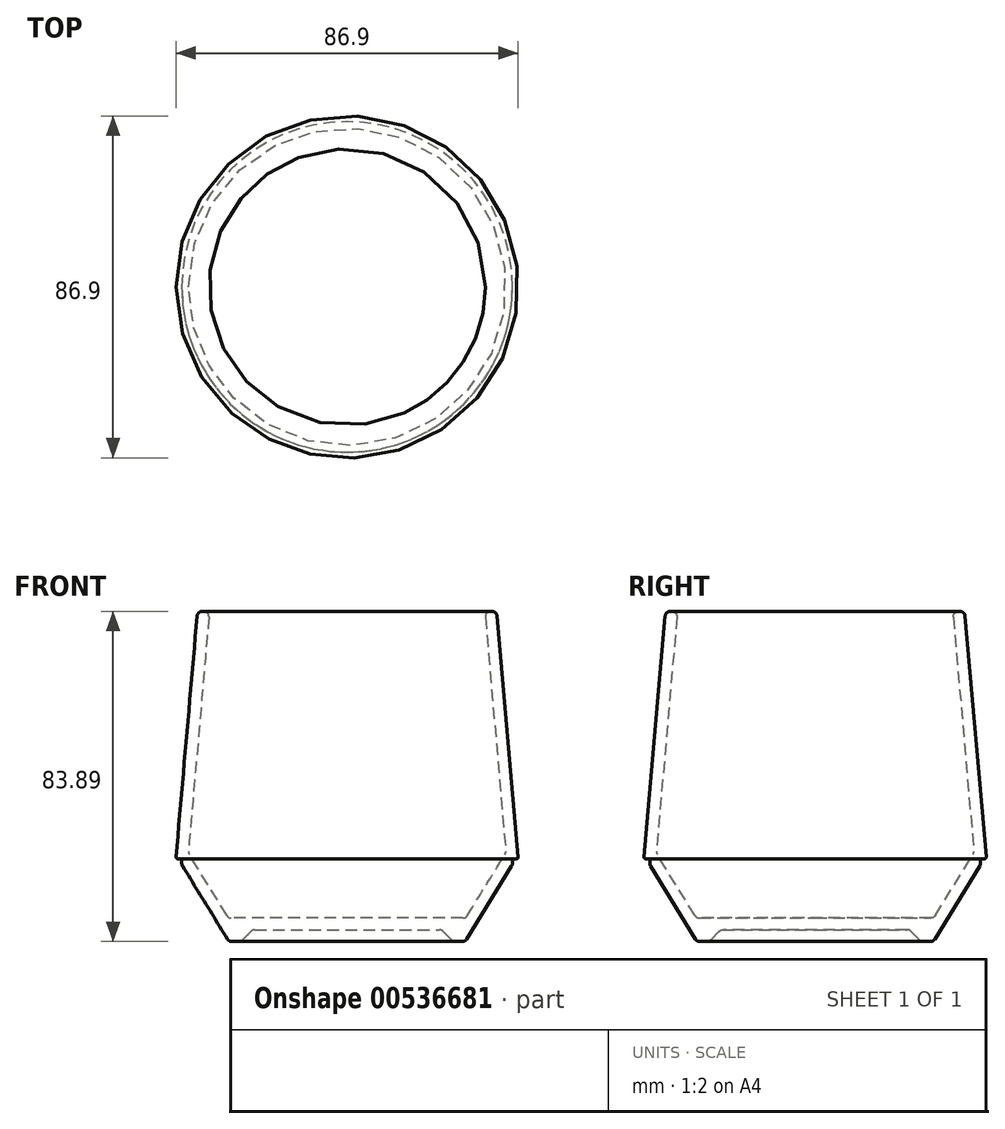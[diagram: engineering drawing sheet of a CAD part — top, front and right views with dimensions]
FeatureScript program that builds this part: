
annotation { "Feature Type Name" : "Feature", "Feature Type Description" : "" }
export const myFeature = defineFeature(function(context is Context, id is Id, definition is map)
    precondition{}
    {
        {
            var Q0;
            Q0=qCreatedBy(makeId("Front.planeOp"),FACE);
            var sketch = newSketch(context, id + "F0", { "sketchPlane" : qUnion([Q0])});
            skLineSegment(sketch, "E0", {"start": v(0, 3) * mm, "end": v(24, 3) * mm});
            skLineSegment(sketch, "E1", {"start": v(24, 3) * mm, "end": v(27, 0) * mm});
            skLineSegment(sketch, "E2", {"start": v(27, 0) * mm, "end": v(30, 0) * mm});
            skLineSegment(sketch, "E3", {"start": v(30, 0) * mm, "end": v(42, 19.5) * mm});
            skLineSegment(sketch, "E4", {"start": v(43.5, 21) * mm, "end": v(37.99, 84) * mm});
            skLineSegment(sketch, "E5", {"start": v(35, 83.74) * mm, "end": v(40.35, 22.55) * mm});
            skLineSegment(sketch, "E6", {"start": v(40.35, 22.55) * mm, "end": v(30.17, 6) * mm});
            skLineSegment(sketch, "E7", {"start": v(30.17, 6) * mm, "end": v(0, 6) * mm});
            skLineSegment(sketch, "E8", {"start": v(0, 6) * mm, "end": v(0, 3) * mm});
            skPoint(sketch, "E9.visualSharp", {"position": v(24, 3) * mm});
            skPoint(sketch, "E10.visualSharp", {"position": v(40.35, 22.55) * mm});
            skLineSegment(sketch, "E11", {"start": v(0, 0) * mm, "end": v(0, 84) * mm, "construction": true});
            skLineSegment(sketch, "E12", {"start": v(42, 19.5) * mm, "end": v(42, 21) * mm});
            skLineSegment(sketch, "E13", {"start": v(43.5, 0) * mm, "end": v(43.5, 84) * mm, "construction": true});
            skLineSegment(sketch, "E14", {"start": v(35, 83.74) * mm, "end": v(37.99, 84) * mm});
            skLineSegment(sketch, "E15", {"start": v(42, 21) * mm, "end": v(43.5, 21) * mm});
            skSolve(sketch);
        }
        {
            var Q0;
            Q0=qSketchRegion(id+"F0",true);
            var Q1;
            Q1=sQuery(id+"F0.wireOp",EDGE,"E11");
            revolve(context, id + "F1", {"entities" : qUnion([Q0]), "axis" : qUnion([Q1]), "revolveType" : RevolveType.FULL});
        }
        {
            var Q0;
            Q0=makeQuery(id+"F1.opRevolve","SWEPT_EDGE",EDGE,{"disambiguationData":[OSD([sQuery(id+"F0.wireOp",EDGE,"E5"),sQuery(id+"F0.wireOp",EDGE,"E14")])]});
            var Q1;
            Q1=makeQuery(id+"F1.opRevolve","SWEPT_EDGE",EDGE,{"disambiguationData":[OSD([sQuery(id+"F0.wireOp",EDGE,"E4"),sQuery(id+"F0.wireOp",EDGE,"E14")])]});
            var Q2;
            Q2=makeQuery(id+"F1.opRevolve","SWEPT_EDGE",EDGE,{"disambiguationData":[OSD([sQuery(id+"F0.wireOp",EDGE,"E5"),sQuery(id+"F0.wireOp",EDGE,"E6")])]});
            var Q3;
            Q3=makeQuery(id+"F1.opRevolve","SWEPT_EDGE",EDGE,{"disambiguationData":[OSD([sQuery(id+"F0.wireOp",EDGE,"E6"),sQuery(id+"F0.wireOp",EDGE,"E7")])]});
            var Q4;
            Q4=makeQuery(id+"F1.opRevolve","SWEPT_EDGE",EDGE,{"disambiguationData":[OSD([sQuery(id+"F0.wireOp",EDGE,"E0"),sQuery(id+"F0.wireOp",EDGE,"E1")])]});
            var Q5;
            Q5=makeQuery(id+"F1.opRevolve","SWEPT_EDGE",EDGE,{"disambiguationData":[OSD([sQuery(id+"F0.wireOp",EDGE,"E1"),sQuery(id+"F0.wireOp",EDGE,"E2")])]});
            var Q6;
            Q6=makeQuery(id+"F1.opRevolve","SWEPT_EDGE",EDGE,{"disambiguationData":[OSD([sQuery(id+"F0.wireOp",EDGE,"E2"),sQuery(id+"F0.wireOp",EDGE,"E3")])]});
            var Q7;
            Q7=makeQuery(id+"F1.opRevolve","SWEPT_EDGE",EDGE,{"disambiguationData":[OSD([sQuery(id+"F0.wireOp",EDGE,"E3"),sQuery(id+"F0.wireOp",EDGE,"E12")])]});
            fillet(context, id + "F2", {"entities" : qUnion([Q0, Q1, Q2, Q3, Q4, Q5, Q6, Q7]), "radius" : 1.3 * mm, "tangentPropagation" : true, "allowEdgeOverflow" : false});
        }
        {
            var Q0;
            Q0=makeQuery(id+"F1.opRevolve","SWEPT_EDGE",EDGE,{"disambiguationData":[OSD([sQuery(id+"F0.wireOp",EDGE,"E12"),sQuery(id+"F0.wireOp",EDGE,"E15")])]});
            var Q1;
            Q1=makeQuery(id+"F1.opRevolve","SWEPT_EDGE",EDGE,{"disambiguationData":[OSD([sQuery(id+"F0.wireOp",EDGE,"E4"),sQuery(id+"F0.wireOp",EDGE,"E15")])]});
            fillet(context, id + "F3", {"entities" : qUnion([Q0, Q1]), "radius" : 0.5 * mm, "tangentPropagation" : true, "allowEdgeOverflow" : false});
        }
    });
